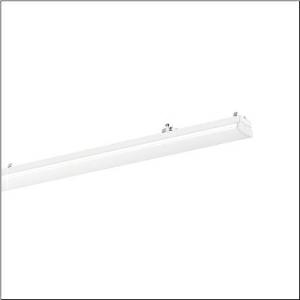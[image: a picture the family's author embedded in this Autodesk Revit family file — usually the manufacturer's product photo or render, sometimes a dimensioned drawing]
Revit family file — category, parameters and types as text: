
# Revit family: licross_11_recessed_opal_mo_51tl1ddn445g
name_source: partatom
category: Lighting Fixtures
units: mm (PartAtom-declared; Revit-internal decimal feet)

## family parameters
Cut with Voids When Loaded = No
Host = Face
Light Source = No
Part Type = Normal
Room Calculation Point = No
Round Connector Dimension = Use Diameter
Shared = No

## types (1)
- --- (1 x LED, 4500 lm, 25.2 W, 4000K)
    Apparent Load = 25 VA
    CIE Flux Codes = 44 73 91 87 100
    Color Rendering = 80
    Color Temperature = 4000K
    Default Elevation = 1800 mm
    Description = Licross 11 recessed opal MO, luminaire insert, of sheet steel, coil coated, white, length: 1.500mm, width: 76mm, height: 87mm, LED rated luminous flux: 4.500lm, light colour: 840, SDCM (Standard Deviation of Colour Matching)MacAdam ≤ 2 SDCM (initial), control gear: DALI 2, with plug, 5-pole, with phase selection, mains connection: 220..240V, AC, 50/60Hz, rated input power: 25W, internal wiring halogen-free, primary optical cover: cover, of PMMA, light emission: direct with ceiling illumination distribution, primary light characteristic: symmetric, protection rating (complete): IP40, insulation class (complete): insulation class I (protective earthing), certification: CE, ENEC, VDE, UKCA, protection symbol: D if used in an environment without relevant dust loads with corresponding accessories, impact resistance: IK06, permissible ambient temperature for indoor applications: -25..+45°C, corresponds to IFS (International Featured Standards) requirements for safety and quality in the food industry, reducing of maximum allowable ambient temperature of 5°C with ceiling mounting, LABS conformity tested according to VDMA 24364:2018-05, The light source and the operating device comply with the requirements of the Ecodesign Regulation (EU) 2019/2020 and are replaceable in accordance with this regulation, packaging unit: 1 piece
    Height = 83 mm
    Lamp = 1 x LED
    Lamp Light Flux = 4500 lm
    Lamp Power = 25.2 W
    Lamp count = 1
    Length = 1500 mm
    Luminous efficacy = 179 lm/W
    Manufacturer = Siteco
    ModVariant = No
    Model = 51TL1DDN445G
    Mounting Place = Ceiling
    Mounting Type = Pendant
    Number of Poles = 1
    OnlyDefault = Yes
    Power Factor = 1
    Product Name = Licross 11 recessed opal MO
    Product group = luminaire insert | ceiling pendant
    ProductGroupID = 901
    Protection Class = Protection class I
    Protection Degree = IP 40
    RLX_Detail_Level = 1
    RLX_Emergency_Light_Flux = 0 lm
    RLX_Emergency_Type = 0
    RLX_Emergency_Type_DB = No
    RlxData = <blob elided: 27181 chars, md5=9b6843df>
    Socket = socket
    Standby Power = 0 W
    System Light Flux = 4500 lm
    System Power = 25 W
    Type Comments = factory setting: luminous flux: 100 % | dim-lin: 254 | 167 mA
    Type Image = l_1313666.jpg
    URL = http://relux.com
    VarID = @adj_083971
    Voltage = 0 V
    Weight = 0.00 kg
    Width = 76 mm

## geometry (parser evidence)
native form markers: Blend x4, Sweep x15
no freeform markers — native parametric forms only
